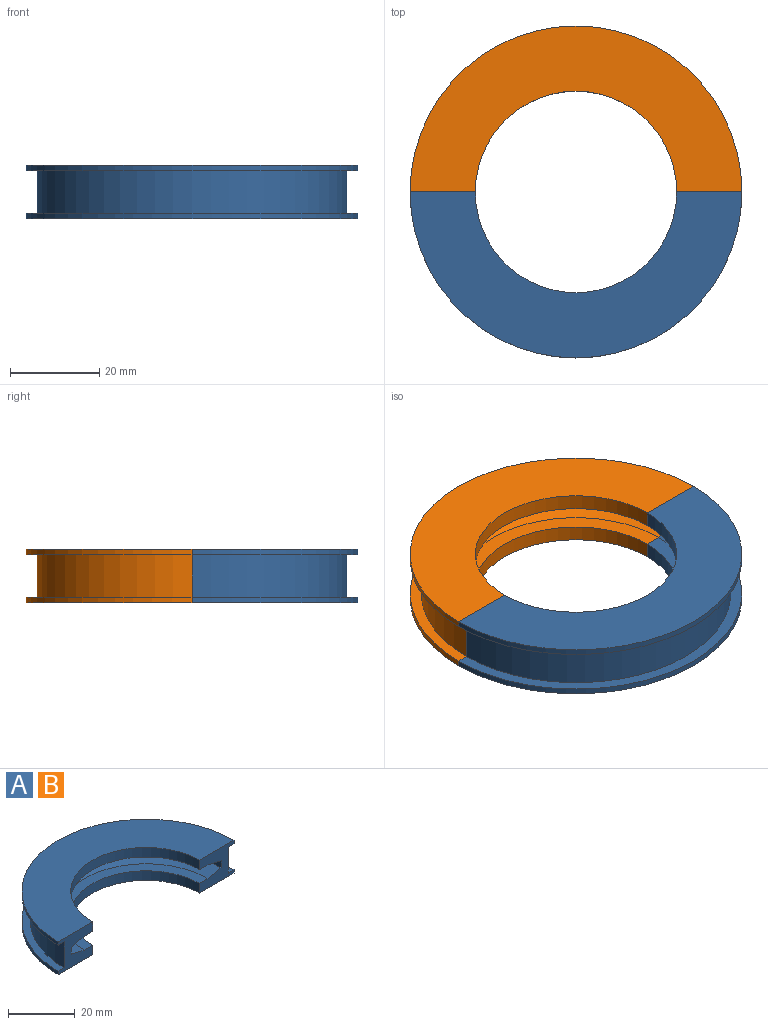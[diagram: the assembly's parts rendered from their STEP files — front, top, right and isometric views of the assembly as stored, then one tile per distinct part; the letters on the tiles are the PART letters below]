
ASSEMBLY  parts=2 mates=1
PART A: 16 faces, bbox 74.5x37.3x12.1 mm
  f0: plane 14.64x12.08mm, normal (0,-1,0), area 113.6mm2, adj f2,f3,f4,f5,f6,f7,f8,f9
  f1: plane 14.64x12.08mm, normal (0,-1,0), area 113.6mm2, adj f2,f3,f4,f5,f6,f7,f8,f9
  f2: cylinder r=22.61mm len=45.21mm, axis (0,0,-1), area 248.6mm2, adj f0,f1,f3,f14
  f3: plane 74.5x37.25mm, normal (0,0,-1), area 1376.9mm2, adj f0,f1,f2,f4
  f4: cylinder r=37.25mm len=74.5mm, axis (0,0,-1), area 149.5mm2, adj f0,f1,f3,f5
  f5: plane 74.5x37.25mm, normal (0,0,1), area 282.7mm2, adj f0,f1,f4,f6
  f6: cylinder r=34.75mm len=69.5mm, axis (0,0,-1), area 1039.8mm2, adj f0,f1,f5,f7
  f7: plane 74.5x37.25mm, normal (0,0,-1), area 282.7mm2, adj f0,f1,f6,f8
  f8: cylinder r=37.25mm len=74.5mm, axis (0,0,-1), area 149.5mm2, adj f0,f1,f7,f9
  f9: plane 74.5x37.25mm, normal (0,0,1), area 1376.9mm2, adj f0,f1,f8,f10
  f10: cylinder r=22.61mm len=45.21mm, axis (0,0,-1), area 248.6mm2, adj f0,f1,f9,f11
  f11: plane 52.5x26.25mm, normal (0,0,-1), area 279.7mm2, adj f0,f1,f10,f12
  f12: cone r=31.75mm half-angle=77deg, axis (0,0,-1), area 514.3mm2, adj f0,f1,f11,f13
  f13: cylinder r=31.75mm len=63.5mm, axis (0,0,-1), area 253.4mm2, adj f0,f1,f12,f15
  f14: plane 52.5x26.25mm, normal (0,0,1), area 279.7mm2, adj f0,f1,f2,f15
  f15: cone r=31.75mm half-angle=77deg, axis (0,0,1), area 514.3mm2, adj f0,f1,f13,f14
PART B: same geometry as A
PLACE A rot(axis=(0,0,1),180deg) t=(-68.21,134.12,84.54)mm
PLACE B t=(-68.21,134.12,84.54)mm
MATE fastened B.f1 <-> A.f0  axis (0,-1,0) through (-105.46,134.12,90.58)mm
